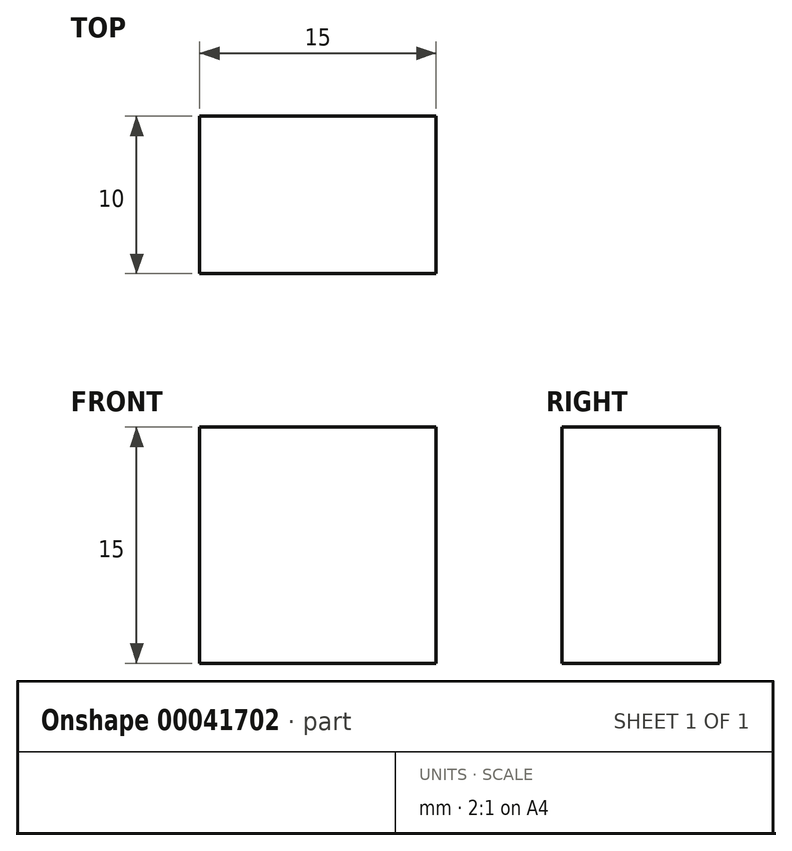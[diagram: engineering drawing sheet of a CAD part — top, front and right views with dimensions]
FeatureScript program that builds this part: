
annotation { "Feature Type Name" : "Feature", "Feature Type Description" : "" }
export const myFeature = defineFeature(function(context is Context, id is Id, definition is map)
    precondition{}
    {
        {
            var Q0;
            Q0=qCreatedBy(makeId("Front.planeOp"),FACE);
            var sketch = newSketch(context, id + "F0", { "sketchPlane" : qUnion([Q0])});
            skLineSegment(sketch, "E0.bottom", {"start": v(0, 0) * mm, "end": v(15, 0) * mm});
            skLineSegment(sketch, "E0.top", {"start": v(0, -15) * mm, "end": v(15, -15) * mm});
            skLineSegment(sketch, "E0.left", {"start": v(0, 0) * mm, "end": v(0, -15) * mm});
            skLineSegment(sketch, "E0.right", {"start": v(15, 0) * mm, "end": v(15, -15) * mm});
            skSolve(sketch);
        }
        {
            var Q0;
            Q0=makeQuery(id+"F0.imprint","IMPRINT",FACE,{"disambiguationData":[TD([[makeQuery(id+"F0.imprint","IMPRINT",EDGE,{"derivedFrom":sQuery(id+"F0.wireOp",EDGE,"E0.bottom")}),-1.0]])]});
            extrude(context, id + "F1", {"entities" : qUnion([Q0]), "depth" : 10 * mm});
        }
    });
